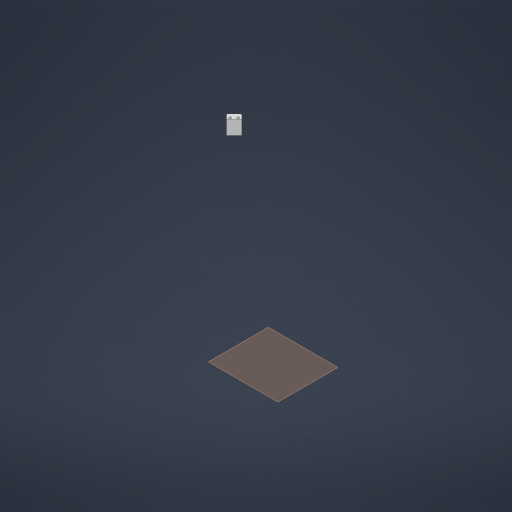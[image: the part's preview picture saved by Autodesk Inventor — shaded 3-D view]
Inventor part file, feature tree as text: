
AUTODESK INVENTOR PART (.ipt)
format: ipt  version: 2023 (Build 270158000, 158)  size: 204,800 bytes
history: native  units: in
note: dims shown in document units (in); Inventor stores cm internally (conversion verified against a paired STEP export)
features: reference x6, other x5, sketch x4, extrude x3, plane x1, hole x1, fillet x1
ambient origin geometry x8: Origin, YZ Plane, XZ Plane, XY Plane, X Axis, Y Axis, Z Axis, Center Point
bodies: Body1 (feature_tree)
feature tree (21):
  plane  "Work Plane1"
  extrude  "Extrusion2"  Depth=0.41in TaperAngle=0.0deg
  hole  "Hole1"  [1 undecoded]
  extrude  "Extrusion3"  [1 undecoded]
  fillet  "Fillet1"  [1 undecoded]
  extrude  "Extrusion4"  [1 undecoded]
  sketch  "Sketch2"  dims[d2=1.6in d3=0.0in]
  reference  "Reference1"
  reference  "Reference2"
  reference  "Reference3"
  reference  "Reference4"
  sketch  "Sketch3"  dims[d4=0.28in d5=0.75in d6=0.375in d7=0.25in d8=0.5635in d9=0.41in d10=0.0in d11=0.41in d12=0.0in]
  reference  "Reference5"
  reference  "Reference6"
  sketch  "Sketch4"  dims[d13=0.125in d14=0.125in]
  sketch  "Sketch5"  dims[d15=1.8125in d16=0.0in]
  other  "<userpath>\Documents\GitHub\SDP-Kepler-1708b\FlyingUGV.iam"
  other  "FlyingUGV.iam"
  other  "Top:1"
  other  "Arm:4"
  other  "Electronics Panel:1"
note: 4 required parameter values undecoded (feature->parameter linkage not recoverable at this tier; creation-order binding heuristic only, values carry confidence <= 0.55)
